# Revit family: Faucet-Lavatory-KOHLER-Memoirs-K-454
name_source: partatom
category: Plumbing Fixtures
revit_build: Autodesk Revit 2015 (Build: 20140606_1530(x64)
units: mm (PartAtom-declared; Revit-internal decimal feet)

## types (8) — shared parameters
ADA Compliant = Yes
Assembly Code = D2020
CW Connection = Yes
Date Modified = 10/10/2017
Default Elevation = 36"
Faucet Hole Spacing = 8"
HW Connection = Yes
Inlet Connector = Inlet Connection
Length = 6"
Manufacturer = KOHLER Co.
MasterFormat 1995 = 15410
MasterFormat 2004 = 22.41.39
Material = Brass Construction
Outlet Connector = Outlet Connection
Pressure = 60.00 psi
Product Documentation Link = http://www.us.kohler.com
Product Name = Memoirs
Product Page URL = http://www.us.kohler.com
Spout Reach = 5"
URL = https://www.us.kohler.com
Vent Connection = No
Waste Connection = No
Width = 13"

## per-type parameters (varying)
| type | Deco Lever Handle | Description | Finish | Flow Rate | Height | Lever Handle | Model | Red & Blue Indexing | Type |
| Deco lever handles, CP-Polished Chrome | Yes | Memoirs Stately widespread bathroom sink faucet with deco lever handles | Kohler-Metal-CP-Polished_Chrome | 1 GPM | 4 1/8" | No | K-454-4V-CP | No | 1 |
| Deco lever handles, BN-Vibrant Brushed Nickel | Yes | Memoirs Stately widespread bathroom sink faucet with deco lever handles | Kohler-Metal-BN-Vibrant_Brushed_Nickel | 1 GPM | 4 1/8" | No | K-454-4V-BN | No | 2 |
| Deco lever handles, BV-Vibrant Brushed Bronze | Yes | Memoirs Stately widespread bathroom sink faucet with deco lever handles | Kohler-Metal-BV-Brushed_Bronze | 1 GPM | 4 1/8" | No | K-454-4V-BV | No | 3 |
| Deco lever handles, 2BZ-Oil Rubbed Bronze | Yes | Memoirs Stately widespread bathroom sink faucet with deco lever handles | Kohler-Metal-2BZ-Oil_Rubbed_Bronze | 1 GPM | 4 1/8" | No | K-454-4V-2BZ | No | 4 |
| Lever handles, CP-Polished Chrome | No | Memoirs Stately widespread bathroom sink faucet with lever handles | Kohler-Metal-CP-Polished_Chrome | 1 GPM | 4 3/16" | Yes | K-454-4S-CP | No | 5 |
| Lever handles, BN-Vibrant Brushed Nickel | No | Memoirs Stately widespread bathroom sink faucet with lever handles | Kohler-Metal-BN-Vibrant_Brushed_Nickel | 1 GPM | 4 3/16" | Yes | K-454-4S-BN | No | 6 |
| Lever handles, BV-Vibrant Brushed Bronze | No | Memoirs Stately widespread bathroom sink faucet with lever handles | Kohler-Metal-BV-Brushed_Bronze | 1 GPM | 4 3/16" | Yes | K-454-4S-BV | No | 7 |
| Red and Blue Indexing and Deco lever handles, CP-Polished Chrome | Yes | Memoirs Stately widespread commercial lavatory faucet with red and blue indexing and Deco lever handles | Kohler-Metal-CP-Polished_Chrome | 2 GPM | 4 1/8" | No | K-454-X4V-CP | Yes | 8 |

## geometry (parser evidence)
native form markers: Blend x4, Sweep x12
no freeform markers — native parametric forms only
